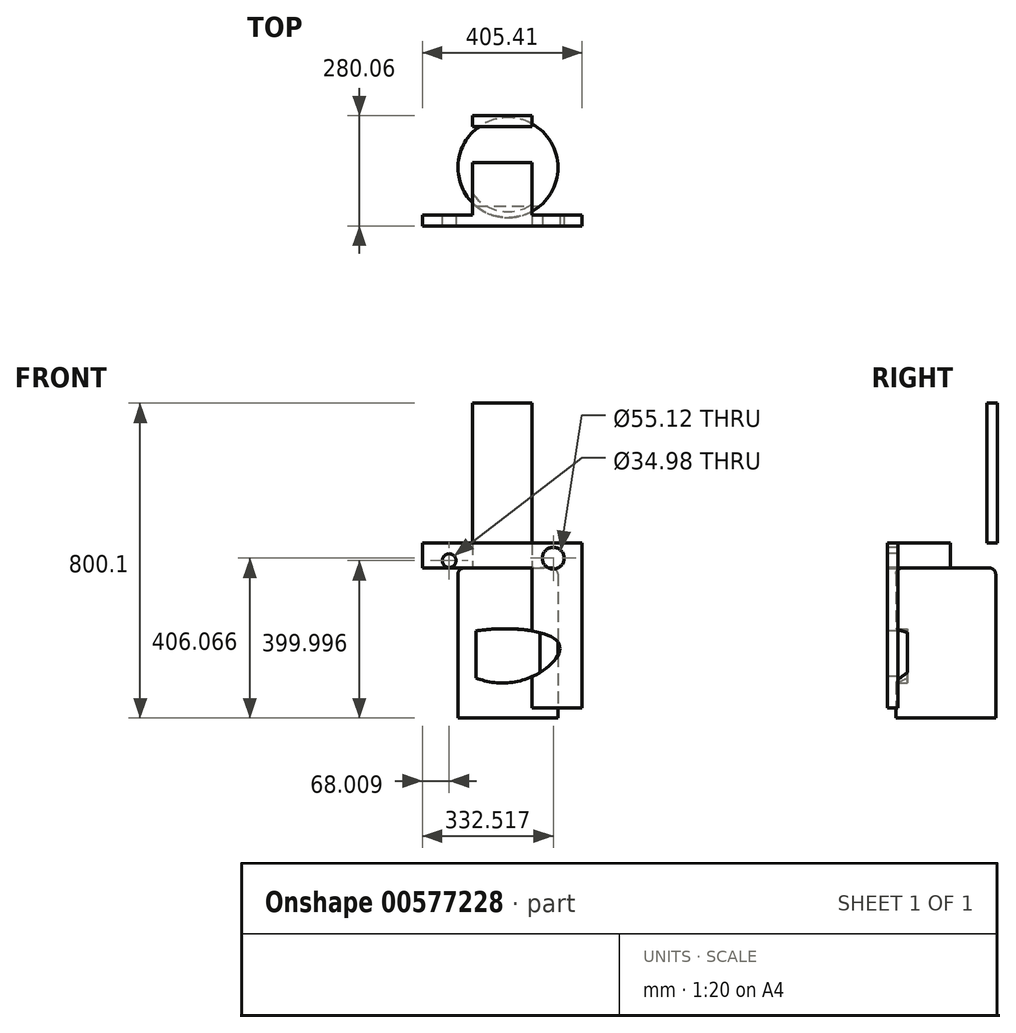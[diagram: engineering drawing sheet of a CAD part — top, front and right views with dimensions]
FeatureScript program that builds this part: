
annotation { "Feature Type Name" : "Feature", "Feature Type Description" : "" }
export const myFeature = defineFeature(function(context is Context, id is Id, definition is map)
    precondition{}
    {
        {
            var Q0;
            Q0=qCreatedBy(makeId("Top.planeOp"),FACE);
            var sketch = newSketch(context, id + "F0", { "sketchPlane" : qUnion([Q0])});
            skCircle(sketch, "E0", {"center": v(-18.03, 8.44) * mm, "radius": 127 * mm});
            skSolve(sketch);
        }
        {
            var Q0;
            Q0 = qSketchRegion(id + "F0", true);
            extrude(context, id + "F1", {"entities" : qUnion([Q0]), "depth" : 381 * mm, "offsetDistance" : 25.4 * mm});
        }
        {
            var Q0;
            Q0=makeQuery(id+"F1.opExtrude","CAP_EDGE",EDGE,{"disambiguationData":[OSD([sQuery(id+"F0.wireOp",EDGE,"E0")])],"isStart":false});
            fillet(context, id + "F2", {"entities" : qUnion([Q0]), "radius" : 15.24 * mm, "tangentPropagation" : true, "allowEdgeOverflow" : false});
        }
        {
            var Q0;
            Q0=makeQuery(id+"F1.opExtrude","CAP_FACE",FACE,{"disambiguationData":[OSD([sQuery(id+"F0.wireOp",EDGE,"E0")])],"isStart":false});
            var sketch = newSketch(context, id + "F3", { "sketchPlane" : qUnion([Q0])});
            skLineSegment(sketch, "E1.bottom", {"start": v(-83.07, 20.74) * mm, "end": v(42.94, 20.74) * mm});
            skLineSegment(sketch, "E1.top", {"start": v(-83.07, -13.03) * mm, "end": v(42.94, -13.03) * mm});
            skLineSegment(sketch, "E1.left", {"start": v(-83.07, 20.74) * mm, "end": v(-83.07, -13.03) * mm});
            skLineSegment(sketch, "E1.right", {"start": v(42.94, 20.74) * mm, "end": v(42.94, -13.03) * mm});
            skSolve(sketch);
        }
        {
            var Q0;
            Q0 = qSketchRegion(id + "F3", true);
            extrude(context, id + "F4", {"entities" : qUnion([Q0]), "operationType" : NewBodyOperationType.ADD, "depth" : 63.5 * mm, "offsetDistance" : 25.4 * mm});
        }
        {
            var Q0;
            Q0=makeQuery(id+"F4.opExtrude","SWEPT_FACE",FACE,{"disambiguationData":[OSD([sQuery(id+"F3.wireOp",EDGE,"E1.top")])]});
            var sketch = newSketch(context, id + "F5", { "sketchPlane" : qUnion([Q0])});
            skSolve(sketch);
        }
        {
            var Q0;
            {var subQ0=sQuery(id+"F3.wireOp",EDGE,"E1.top");Q0=makeQuery(id+"F5.imprint","IMPRINT",FACE,{"disambiguationData":[TD([[makeQuery(id+"F5.imprint","IMPRINT",EDGE,{"derivedFrom":makeQuery(id+"F4.opExtrude","CAP_EDGE",EDGE,{"disambiguationData":[OSD([subQ0])],"isStart":false})}),-1.0]])]});}
            extrude(context, id + "F6", {"entities" : qUnion([Q0]), "operationType" : NewBodyOperationType.ADD, "depth" : 127 * mm, "offsetDistance" : 25.4 * mm});
        }
        {
            var Q0;
            {var subQ0=sQuery(id+"F3.wireOp",EDGE,"E1.top");Q0=makeQuery(id+"F6.opExtrude","SWEPT_FACE",FACE,{"disambiguationData":[OSD([subQ0]),TDD([makeQuery(id+"F5.imprint","IMPRINT",EDGE,{"derivedFrom":makeQuery(id+"F4.opExtrude","CAP_EDGE",EDGE,{"disambiguationData":[OSD([subQ0])],"isStart":true})})])]});}
            var sketch = newSketch(context, id + "F7", { "sketchPlane" : qUnion([Q0])});
            skLineSegment(sketch, "E2.bottom", {"start": v(-83.07, 140.03) * mm, "end": v(42.94, 140.03) * mm});
            skLineSegment(sketch, "E2.top", {"start": v(-83.07, 112.63) * mm, "end": v(42.94, 112.63) * mm});
            skLineSegment(sketch, "E2.left", {"start": v(-83.07, 140.03) * mm, "end": v(-83.07, 112.63) * mm});
            skLineSegment(sketch, "E2.right", {"start": v(42.94, 140.03) * mm, "end": v(42.94, 112.63) * mm});
            skSolve(sketch);
        }
        {
            var Q0;
            Q0 = qSketchRegion(id + "F7", true);
            extrude(context, id + "F8", {"entities" : qUnion([Q0]), "operationType" : NewBodyOperationType.ADD, "depth" : 355.6 * mm, "offsetDistance" : 25.4 * mm});
        }
        {
            var Q0;
            {var subQ0=sQuery(id+"F3.wireOp",EDGE,"E1.left");Q0=makeQuery(id+"F8.boolean.opBoolean","MERGE",FACE,{"derivedFrom":[makeQuery(id+"F6.boolean.opBoolean","MERGE",FACE,{"derivedFrom":[makeQuery(id+"F4.opExtrude","SWEPT_FACE",FACE,{"disambiguationData":[OSD([subQ0])]}),makeQuery(id+"F6.opExtrude","SWEPT_FACE",FACE,{"disambiguationData":[OSD([sQuery(id+"F3.wireOp",EDGE,"E1.top"),subQ0])]})]}),makeQuery(id+"F8.opExtrude","SWEPT_FACE",FACE,{"disambiguationData":[OSD([sQuery(id+"F7.wireOp",EDGE,"E2.left")])]})]});}
            extrude(context, id + "F9", {"entities" : qUnion([Q0]), "operationType" : NewBodyOperationType.ADD, "depth" : 25.4 * mm, "offsetDistance" : 25.4 * mm});
        }
        {
            var Q0;
            Q0=makeQuery(id+"F9.opExtrude","CAP_FACE",FACE,{"disambiguationData":[OSD([sQuery(id+"F3.wireOp",EDGE,"E1.top"),sQuery(id+"F3.wireOp",EDGE,"E1.left"),sQuery(id+"F7.wireOp",EDGE,"E2.left")])],"isStart":false});
            var sketch = newSketch(context, id + "F10", { "sketchPlane" : qUnion([Q0])});
            skLineSegment(sketch, "E3.bottom", {"start": v(140.03, 444.5) * mm, "end": v(112.63, 444.5) * mm});
            skLineSegment(sketch, "E3.top", {"start": v(140.03, 25.4) * mm, "end": v(112.63, 25.4) * mm});
            skLineSegment(sketch, "E3.left", {"start": v(140.03, 444.5) * mm, "end": v(140.03, 25.4) * mm});
            skLineSegment(sketch, "E3.right", {"start": v(112.63, 444.5) * mm, "end": v(112.63, 25.4) * mm});
            skSolve(sketch);
        }
        {
            var Q0;
            {var subQ9=sQuery(id+"F10.wireOp",EDGE,"E3.bottom");Q0=makeQuery(id+"F10.imprint","IMPRINT",FACE,{"disambiguationData":[TD([[makeQuery(id+"F10.imprint","IMPRINT",EDGE,{"derivedFrom":subQ9}),-1.0]])]});}
            extrude(context, id + "F11", {"entities" : qUnion([Q0]), "operationType" : NewBodyOperationType.ADD, "depth" : 127 * mm, "offsetDistance" : 25.4 * mm});
        }
        {
            var Q0;
            {var subQ0=sQuery(id+"F3.wireOp",EDGE,"E1.right");Q0=makeQuery(id+"F8.boolean.opBoolean","MERGE",FACE,{"derivedFrom":[makeQuery(id+"F6.boolean.opBoolean","MERGE",FACE,{"derivedFrom":[makeQuery(id+"F4.opExtrude","SWEPT_FACE",FACE,{"disambiguationData":[OSD([subQ0])]}),makeQuery(id+"F6.opExtrude","SWEPT_FACE",FACE,{"disambiguationData":[OSD([sQuery(id+"F3.wireOp",EDGE,"E1.top"),subQ0])]})]}),makeQuery(id+"F8.opExtrude","SWEPT_FACE",FACE,{"disambiguationData":[OSD([sQuery(id+"F7.wireOp",EDGE,"E2.right")])]})]});}
            var sketch = newSketch(context, id + "F12", { "sketchPlane" : qUnion([Q0])});
            skLineSegment(sketch, "E4.bottom", {"start": v(-112.63, 25.4) * mm, "end": v(-140.03, 25.4) * mm});
            skLineSegment(sketch, "E4.top", {"start": v(-112.63, 444.5) * mm, "end": v(-140.03, 444.5) * mm});
            skLineSegment(sketch, "E4.left", {"start": v(-112.63, 25.4) * mm, "end": v(-112.63, 444.5) * mm});
            skLineSegment(sketch, "E4.right", {"start": v(-140.03, 25.4) * mm, "end": v(-140.03, 444.5) * mm});
            skSolve(sketch);
        }
        {
            var Q0;
            Q0 = qSketchRegion(id + "F12", true);
            extrude(context, id + "F13", {"entities" : qUnion([Q0]), "operationType" : NewBodyOperationType.ADD, "depth" : 127 * mm, "offsetDistance" : 25.4 * mm});
        }
        {
            var Q0;
            {var subQ0=sQuery(id+"F7.wireOp",EDGE,"E2.bottom");var subQ1=sQuery(id+"F3.wireOp",EDGE,"E1.left");var subQ2=sQuery(id+"F3.wireOp",EDGE,"E1.top");Q0=makeQuery(id+"F13.boolean.opBoolean","MERGE",FACE,{"derivedFrom":[makeQuery(id+"F11.boolean.opBoolean","MERGE",FACE,{"derivedFrom":[makeQuery(id+"F9.boolean.opBoolean","MERGE",FACE,{"derivedFrom":[makeQuery(id+"F8.boolean.opBoolean","MERGE",FACE,{"derivedFrom":[makeQuery(id+"F6.opExtrude","CAP_FACE",FACE,{"disambiguationData":[OSD([subQ2,subQ1,sQuery(id+"F3.wireOp",EDGE,"E1.right")])],"isStart":false}),makeQuery(id+"F8.opExtrude","SWEPT_FACE",FACE,{"disambiguationData":[OSD([subQ0])]})]}),makeQuery(id+"F9.opExtrude","SWEPT_FACE",FACE,{"disambiguationData":[OSD([subQ2,subQ1,subQ0,sQuery(id+"F7.wireOp",EDGE,"E2.left")])]})]}),makeQuery(id+"F11.opExtrude","SWEPT_FACE",FACE,{"disambiguationData":[OSD([sQuery(id+"F10.wireOp",EDGE,"E3.left")])]})]}),makeQuery(id+"F13.opExtrude","SWEPT_FACE",FACE,{"disambiguationData":[OSD([sQuery(id+"F12.wireOp",EDGE,"E4.right")])]})]});}
            var sketch = newSketch(context, id + "F14", { "sketchPlane" : qUnion([Q0])});
            skCircle(sketch, "E5", {"center": v(-167.46, 400) * mm, "radius": 17.49 * mm});
            skCircle(sketch, "E6", {"center": v(97.05, 406.07) * mm, "radius": 27.56 * mm});
            skFitSpline(sketch, "E7", {"points": [v(-176.03, 189.04) * mm, v(-26.73, 88.95) * mm, v(108, 194.15) * mm, v(-176.03, 189.04) * mm]});
            skSolve(sketch);
        }
        {
            var Q0;
            Q0 = qSketchRegion(id + "F14", true);
            extrude(context, id + "F15", {"entities" : qUnion([Q0]), "operationType" : NewBodyOperationType.REMOVE, "oppositeDirection" : true, "depth" : 50.8 * mm, "offsetDistance" : 25.4 * mm});
        }
    });
